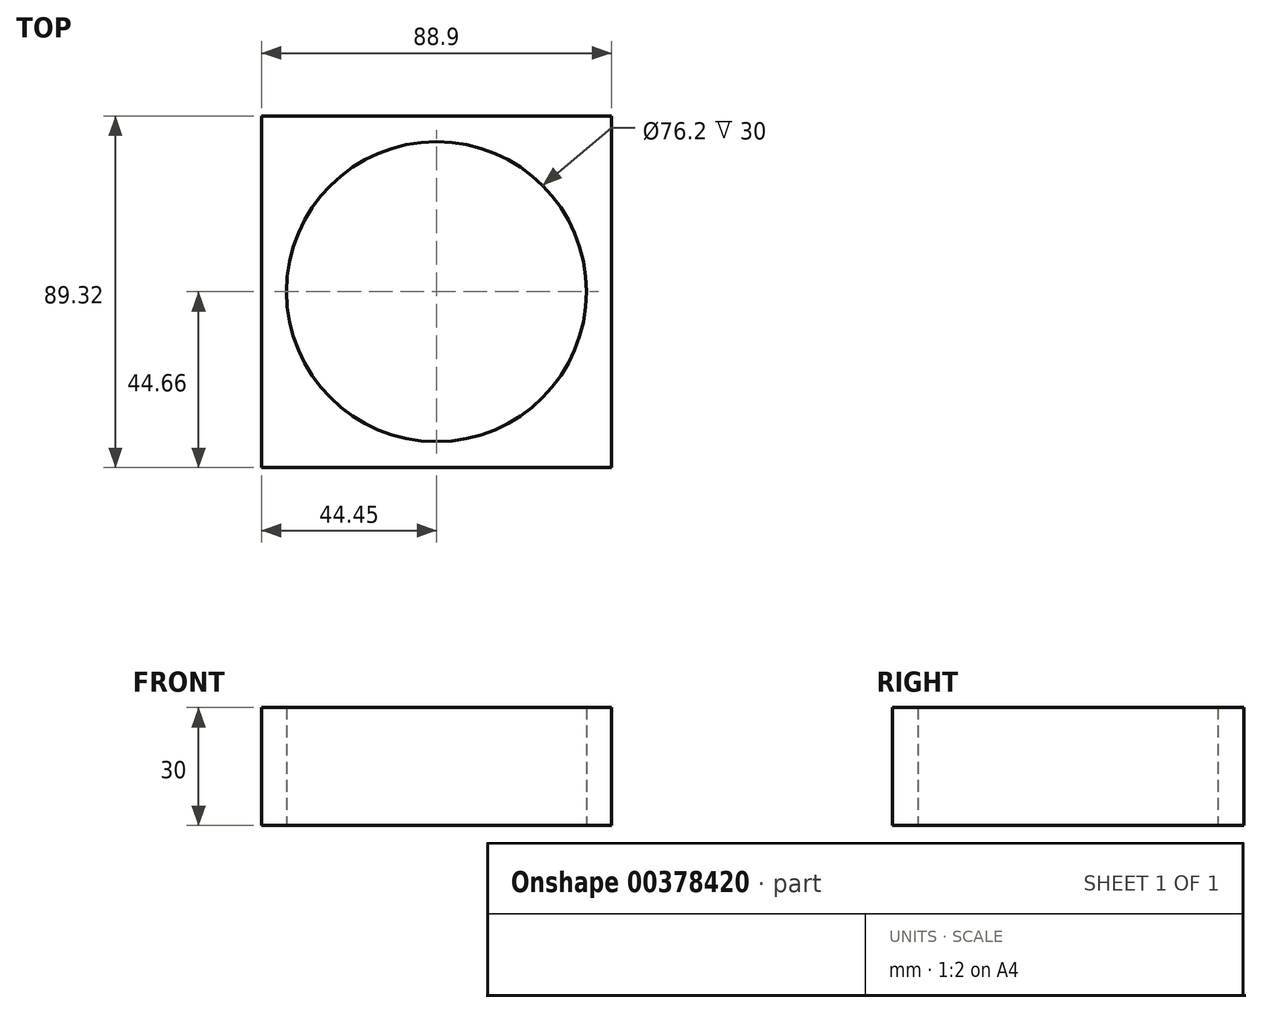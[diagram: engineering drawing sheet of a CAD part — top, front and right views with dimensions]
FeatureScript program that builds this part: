
annotation { "Feature Type Name" : "Feature", "Feature Type Description" : "" }
export const myFeature = defineFeature(function(context is Context, id is Id, definition is map)
    precondition{}
    {
        {
            var Q0;
            Q0=qCreatedBy(makeId("Top.planeOp"),FACE);
            var sketch = newSketch(context, id + "F0", { "sketchPlane" : qUnion([Q0])});
            skPoint(sketch, "E0.middle", {"position": v(0, 0) * mm});
            skLineSegment(sketch, "E1.bottom", {"start": v(-44.45, -44.66) * mm, "end": v(44.45, -44.66) * mm});
            skLineSegment(sketch, "E1.top", {"start": v(-44.45, 44.66) * mm, "end": v(44.45, 44.66) * mm});
            skLineSegment(sketch, "E1.left", {"start": v(-44.45, -44.66) * mm, "end": v(-44.45, 44.66) * mm});
            skLineSegment(sketch, "E1.right", {"start": v(44.45, -44.66) * mm, "end": v(44.45, 44.66) * mm});
            skCircle(sketch, "E2", {"center": v(0, 0) * mm, "radius": 38.1 * mm});
            skSolve(sketch);
        }
        {
            var Q0;
            Q0 = qSketchRegion(id + "F0", true);
            extrude(context, id + "F1", {"entities" : qUnion([Q0]), "depth" : 30 * mm});
        }
    });
